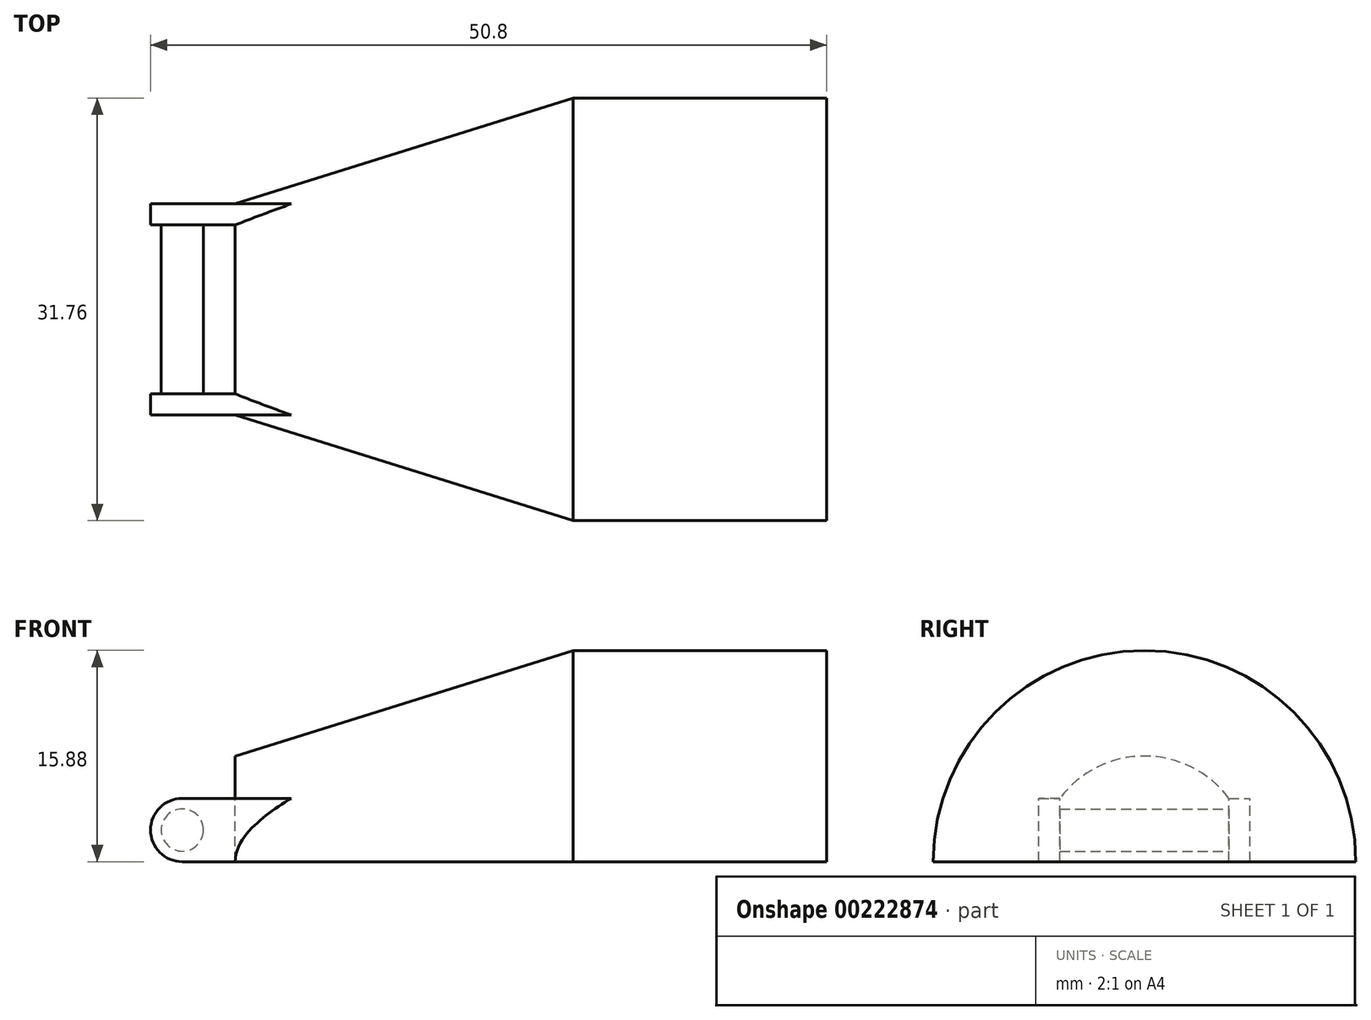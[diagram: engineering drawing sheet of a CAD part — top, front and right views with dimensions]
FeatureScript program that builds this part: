
annotation { "Feature Type Name" : "Feature", "Feature Type Description" : "" }
export const myFeature = defineFeature(function(context is Context, id is Id, definition is map)
    precondition{}
    {
        {
            var Q0;
            Q0=qCreatedBy(makeId("Right.planeOp"),FACE);
            var sketch = newSketch(context, id + "F0", { "sketchPlane" : qUnion([Q0])});
            skLineSegment(sketch, "E0", {"start": v(-15.88, 0) * mm, "end": v(15.88, 0) * mm});
            skCircle(sketch, "E1", {"center": v(0, 0) * mm, "radius": 15.88 * mm});
            skSolve(sketch);
        }
        {
            var Q0;
            Q0=qCreatedBy(makeId("Right.planeOp"),FACE);
            cPlane(context, id + "F1", {"entities" : qUnion([Q0]), "cplaneType" : CPlaneType.OFFSET, "offset" : 25.4 * mm, "oppositeDirection" : true, "width" : 152.4 * mm, "height" : 152.4 * mm});
        }
        {
            var Q0;
            Q0=qCreatedBy(id+"F1.planeOp",FACE);
            var sketch = newSketch(context, id + "F2", { "sketchPlane" : qUnion([Q0])});
            skCircle(sketch, "E2", {"center": v(0, 0) * mm, "radius": 7.94 * mm});
            skLineSegment(sketch, "E3", {"start": v(-7.94, 0) * mm, "end": v(7.94, 0) * mm});
            skSolve(sketch);
        }
        {
            var Q0;
            {var subQ0=sQuery(id+"F2.wireOp",EDGE,"E3");Q0=makeQuery(id+"F2.imprint","IMPRINT",FACE,{"disambiguationData":[TD([[makeQuery(id+"F2.imprint","IMPRINT",EDGE,{"derivedFrom":subQ0}),1.0]])]});}
            var Q1;
            {var subQ0=sQuery(id+"F0.wireOp",EDGE,"E0");Q1=makeQuery(id+"F0.imprint","IMPRINT",FACE,{"disambiguationData":[TD([[makeQuery(id+"F0.imprint","IMPRINT",EDGE,{"derivedFrom":subQ0}),1.0]])]});}
            loft(context, id + "F3", {"sheetProfilesArray" : [{ "sheetProfileEntities" : qUnion([Q0]) }, { "sheetProfileEntities" : qUnion([Q1]) }]});
        }
        {
            var Q0;
            {var subQ0=sQuery(id+"F0.wireOp",EDGE,"E0");Q0=makeQuery(id+"F3.opLoft","CAP_FACE",FACE,{"disambiguationData":[OSD([makeQuery(id+"F0.imprint","IMPRINT",FACE,{"disambiguationData":[TD([[makeQuery(id+"F0.imprint","IMPRINT",EDGE,{"derivedFrom":subQ0}),1.0]])]})])],"isStart":true});}
            extrude(context, id + "F4", {"entities" : qUnion([Q0]), "operationType" : NewBodyOperationType.ADD, "depth" : 19.05 * mm});
        }
        {
            var Q0;
            {var subQ0=sQuery(id+"F2.wireOp",EDGE,"E3");Q0=makeQuery(id+"F3.opLoft","CAP_FACE",FACE,{"disambiguationData":[OSD([makeQuery(id+"F2.imprint","IMPRINT",FACE,{"disambiguationData":[TD([[makeQuery(id+"F2.imprint","IMPRINT",EDGE,{"derivedFrom":subQ0}),1.0]])]})])],"isStart":true});}
            var sketch = newSketch(context, id + "F5", { "sketchPlane" : qUnion([Q0])});
            skLineSegment(sketch, "E4.bottom", {"start": v(-7.94, 0) * mm, "end": v(-6.35, 0) * mm});
            skLineSegment(sketch, "E4.top", {"start": v(-7.94, 4.76) * mm, "end": v(-6.35, 4.76) * mm});
            skLineSegment(sketch, "E4.left", {"start": v(-7.94, 0) * mm, "end": v(-7.94, 4.76) * mm});
            skLineSegment(sketch, "E4.right", {"start": v(-6.35, 0) * mm, "end": v(-6.35, 4.76) * mm});
            skPoint(sketch, "E5.endSnap0", {"position": v(0, 0) * mm});
            skLineSegment(sketch, "E6.MirrorCS", {"start": v(7.94, 0) * mm, "end": v(6.35, 0) * mm});
            skLineSegment(sketch, "E7.MirrorCS", {"start": v(7.94, 0) * mm, "end": v(7.94, 4.76) * mm});
            skLineSegment(sketch, "E8.MirrorCS", {"start": v(6.35, 0) * mm, "end": v(6.35, 4.76) * mm});
            skLineSegment(sketch, "E9.MirrorCS", {"start": v(7.94, 4.76) * mm, "end": v(6.35, 4.76) * mm});
            skSolve(sketch);
        }
        {
            var Q0;
            Q0 = qSketchRegion(id + "F5", true);
            extrude(context, id + "F6", {"entities" : qUnion([Q0]), "operationType" : NewBodyOperationType.ADD, "endBound" : BoundingType.SYMMETRIC, "depth" : 12.7 * mm});
        }
        {
            var Q0;
            Q0=makeQuery(id+"F6.opExtrude","SWEPT_FACE",FACE,{"disambiguationData":[OSD([sQuery(id+"F5.wireOp",EDGE,"E4.left")])]});
            var sketch = newSketch(context, id + "F7", { "sketchPlane" : qUnion([Q0])});
            skPoint(sketch, "E10", {"position": v(31.75, 2.38) * mm});
            skLineSegment(sketch, "E11", {"start": v(31.75, 2.38) * mm, "end": v(29.37, 2.38) * mm});
            skCircle(sketch, "E12", {"center": v(29.37, 2.38) * mm, "radius": 2.38 * mm});
            skCircle(sketch, "E13", {"center": v(29.37, 2.38) * mm, "radius": 1.59 * mm});
            skSolve(sketch);
        }
        {
            var Q0;
            {var subQ0=sQuery(id+"F7.wireOp",EDGE,"E12");var subQ1=sQuery(id+"F5.wireOp",EDGE,"E4.left");var subQ2=makeQuery(id+"F6.opExtrude","CAP_EDGE",EDGE,{"disambiguationData":[OSD([subQ1])],"isStart":false});var subQ3=makeQuery(id+"F7.imprint","INTERSECT",VERTEX,{"derivedFrom":[subQ2,subQ0]});Q0=makeQuery(id+"F7.imprint","IMPRINT",FACE,{"disambiguationData":[TD([[makeQuery(id+"F7.imprint","IMPRINT",EDGE,{"disambiguationData":[TD([[subQ3,-1.0]])],"derivedFrom":subQ0}),-1.0]])]});}
            var Q1;
            {var subQ0=sQuery(id+"F7.wireOp",EDGE,"E12");var subQ1=sQuery(id+"F5.wireOp",EDGE,"E4.left");var subQ2=makeQuery(id+"F6.opExtrude","CAP_EDGE",EDGE,{"disambiguationData":[OSD([subQ1])],"isStart":false});var subQ3=makeQuery(id+"F7.imprint","INTERSECT",VERTEX,{"derivedFrom":[subQ2,subQ0]});Q1=makeQuery(id+"F7.imprint","IMPRINT",FACE,{"disambiguationData":[TD([[makeQuery(id+"F7.imprint","IMPRINT",EDGE,{"disambiguationData":[TD([[subQ3,1.0]])],"derivedFrom":subQ0}),-1.0]])]});}
            extrude(context, id + "F8", {"entities" : qUnion([Q0, Q1]), "operationType" : NewBodyOperationType.REMOVE, "oppositeDirection" : true, "depth" : 25.4 * mm});
        }
        {
            var Q0;
            Q0=makeQuery(id+"F7.imprint","IMPRINT",FACE,{"disambiguationData":[TD([[makeQuery(id+"F7.imprint","IMPRINT",EDGE,{"derivedFrom":sQuery(id+"F7.wireOp",EDGE,"E13")}),1.0]])]});
            extrude(context, id + "F9", {"entities" : qUnion([Q0]), "operationType" : NewBodyOperationType.ADD, "oppositeDirection" : true, "depth" : 15.88 * mm});
        }
    });
